# Revit family: LCC8LED-Wall Mount
name_source: partatom
category: Lighting Fixtures
revit_build: Autodesk Revit MEP 2012 (Build: 20110309_2315(x64)
units: mm (PartAtom-declared; Revit-internal decimal feet)

## types (5) — shared parameters
Apparent Load = 0 VA
Default Elevation = 48.000"
Description = 8in LED Wall Mount Cylinder
Glass = Hubbell - White Glass
Lamp = LED Lamp
Load Classification = Lighting
Manufacturer = Prescolite
Manufacturer Fax = 866-898-0131
Model = LCC8LED
URL = http://www.prescolite.com
Voltage = 120 V
Wattage Comments = 40W

## per-type parameters (varying)
| type | Backbox | Photometric Web |
| LCC8LED-Matte White | Hubbell - Matt White | Web LCC8LED : LCC8LEDS10L30K8WFL45 |
| LCC8LED-Matte Black | Hubbell - Matte Black | Web LCC8LED : LCC8LEDS18L30K8WFL45 |
| LCC8LED-Bronze | Hubbell - Bronze | Web LCC8LED : LCC8LEDS24L35K8WFL45 |
| LCC8LED-Brushed Aluminium | Hubbell - Brushed Aluminum | Web LCC8LED : LCC8LEDS10L30K8WFL45 |
| LCC8LED-Zet | Hubbell - Zet | Web LCC8LED : LCC8LEDS10L30K8WFL45 |

## geometry (parser evidence)
native form markers: Sweep x3
no freeform markers — native parametric forms only
